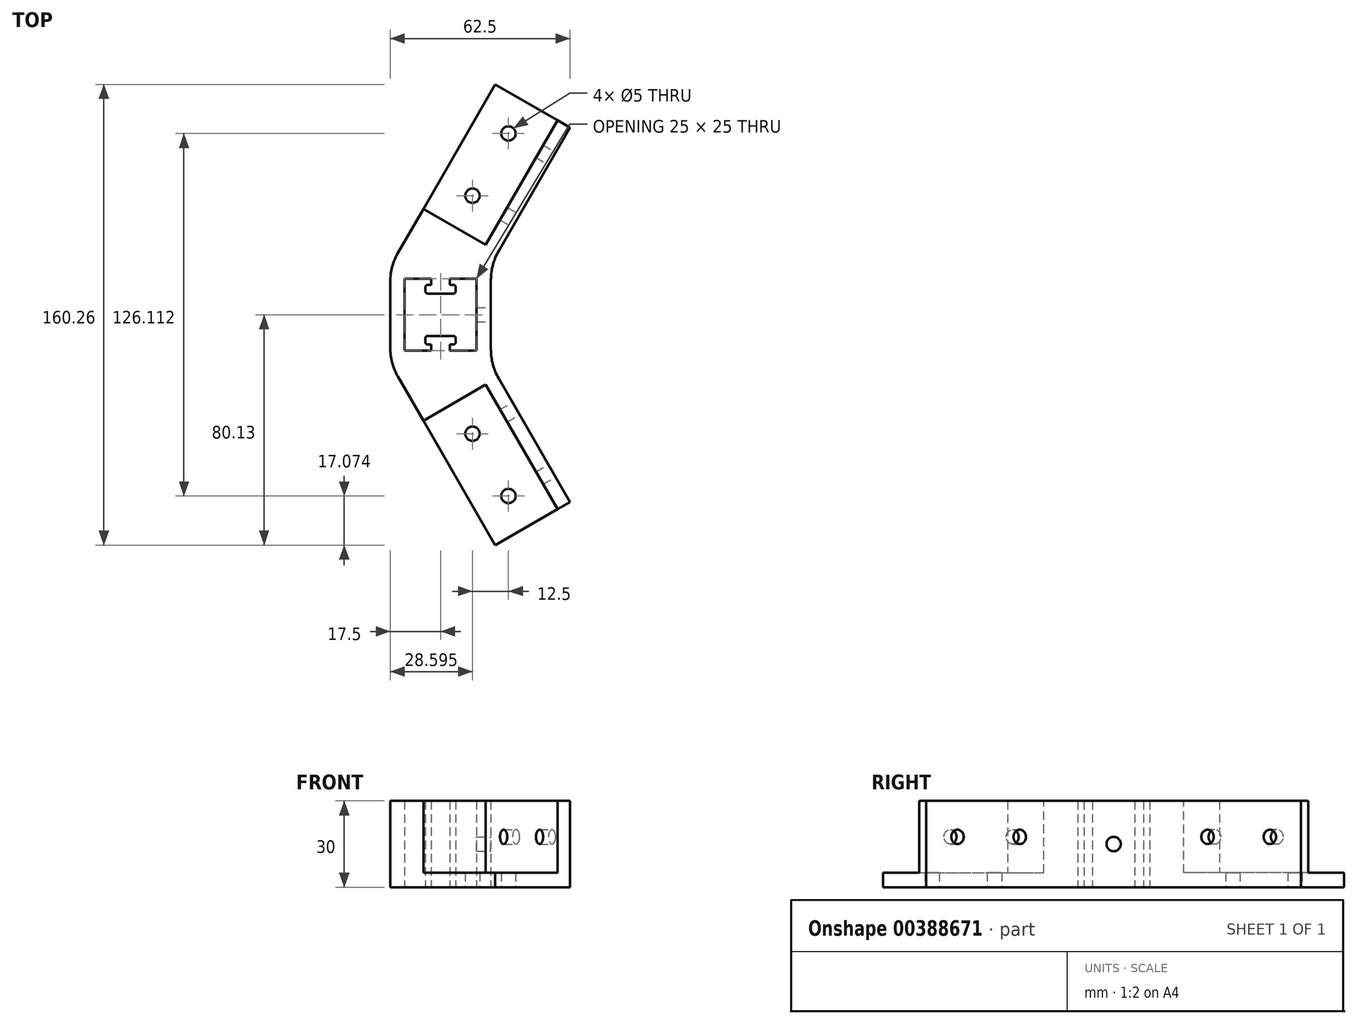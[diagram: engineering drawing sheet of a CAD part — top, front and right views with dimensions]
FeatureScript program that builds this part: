
annotation { "Feature Type Name" : "Feature", "Feature Type Description" : "" }
export const myFeature = defineFeature(function(context is Context, id is Id, definition is map)
    precondition{}
    {
        {
            var Q0;
            Q0=qCreatedBy(makeId("Top.planeOp"),FACE);
            var sketch = newSketch(context, id + "F0", { "sketchPlane" : qUnion([Q0])});
            skLineSegment(sketch, "E0", {"start": v(-35, 0) * mm, "end": v(-35, 16.88) * mm});
            skLineSegment(sketch, "E1", {"start": v(-35, 16.88) * mm, "end": v(-23.48, 36.83) * mm});
            skLineSegment(sketch, "E2", {"start": v(2.5, 21.83) * mm, "end": v(0, 17.5) * mm});
            skLineSegment(sketch, "E3", {"start": v(0, 17.5) * mm, "end": v(0, 0) * mm});
            skLineSegment(sketch, "E4", {"start": v(0, 0) * mm, "end": v(-5, 0) * mm});
            skLineSegment(sketch, "E5", {"start": v(0, 17.5) * mm, "end": v(-25.98, 32.5) * mm, "construction": true});
            skLineSegment(sketch, "E6", {"start": v(-35, 16.88) * mm, "end": v(0, 17.5) * mm, "construction": true});
            skLineSegment(sketch, "E7", {"start": v(0, 17.5) * mm, "end": v(-35, 17.5) * mm, "construction": true});
            skLineSegment(sketch, "E8", {"start": v(2.5, 21.83) * mm, "end": v(-23.48, 36.83) * mm});
            skLineSegment(sketch, "E9", {"start": v(-30, 0) * mm, "end": v(-30, 12.5) * mm});
            skLineSegment(sketch, "E10", {"start": v(-30, 12.5) * mm, "end": v(-20.75, 12.5) * mm});
            skLineSegment(sketch, "E11", {"start": v(-5, 12.5) * mm, "end": v(-5, 0) * mm});
            skLineSegment(sketch, "E12.trimOffspring", {"start": v(-30, 0) * mm, "end": v(-35, 0) * mm});
            skLineSegment(sketch, "E13", {"start": v(-20.75, 12.5) * mm, "end": v(-20.75, 10.37) * mm});
            skLineSegment(sketch, "E14", {"start": v(-20.75, 10.37) * mm, "end": v(-22, 10.37) * mm});
            skLineSegment(sketch, "E15", {"start": v(-22.75, 9.62) * mm, "end": v(-22.75, 8.12) * mm});
            skLineSegment(sketch, "E16", {"start": v(-22, 7.37) * mm, "end": v(-13, 7.37) * mm});
            skLineSegment(sketch, "E17", {"start": v(-12.25, 8.12) * mm, "end": v(-12.25, 9.62) * mm});
            skLineSegment(sketch, "E18", {"start": v(-13, 10.37) * mm, "end": v(-14.25, 10.37) * mm});
            skLineSegment(sketch, "E19", {"start": v(-14.25, 10.37) * mm, "end": v(-14.25, 12.5) * mm});
            skLineSegment(sketch, "E20.trimOffspring", {"start": v(-14.25, 12.5) * mm, "end": v(-5, 12.5) * mm});
            skPoint(sketch, "E21.visualSharp", {"position": v(-22.75, 10.37) * mm});
            skArc(sketch, "E21.filletArc", {"start": v(-22, 10.37) * mm, "mid": v(-22.53, 10.15) * mm, "end": v(-22.75, 9.62) * mm});
            skPoint(sketch, "E22.visualSharp", {"position": v(-22.75, 7.37) * mm});
            skArc(sketch, "E22.filletArc", {"start": v(-22.75, 8.12) * mm, "mid": v(-22.53, 7.59) * mm, "end": v(-22, 7.37) * mm});
            skPoint(sketch, "E23.visualSharp", {"position": v(-12.25, 10.37) * mm});
            skArc(sketch, "E23.filletArc", {"start": v(-12.25, 9.62) * mm, "mid": v(-12.47, 10.15) * mm, "end": v(-13, 10.37) * mm});
            skPoint(sketch, "E24.visualSharp", {"position": v(-12.25, 7.37) * mm});
            skArc(sketch, "E24.filletArc", {"start": v(-13, 7.37) * mm, "mid": v(-12.47, 7.59) * mm, "end": v(-12.25, 8.12) * mm});
            skSolve(sketch);
        }
        {
            var Q0;
            Q0=qSketchRegion(id+"F0",true);
            extrude(context, id + "F1", {"entities" : qUnion([Q0]), "depth" : 30 * mm});
        }
        {
            var Q0;
            Q0=makeQuery(id+"F1.opExtrude","SWEPT_FACE",FACE,{"disambiguationData":[OSD([sQuery(id+"F0.wireOp",EDGE,"E8")])]});
            var sketch = newSketch(context, id + "F2", { "sketchPlane" : qUnion([Q0])});
            skLineSegment(sketch, "E25", {"start": v(8.75, 30) * mm, "end": v(8.75, 0) * mm});
            skLineSegment(sketch, "E26", {"start": v(8.75, 0) * mm, "end": v(38.75, 0) * mm});
            skLineSegment(sketch, "E27", {"start": v(38.75, 0) * mm, "end": v(38.75, 5) * mm});
            skLineSegment(sketch, "E28", {"start": v(38.75, 5) * mm, "end": v(13.75, 5) * mm});
            skLineSegment(sketch, "E29", {"start": v(13.75, 5) * mm, "end": v(13.75, 30) * mm});
            skLineSegment(sketch, "E30", {"start": v(13.75, 30) * mm, "end": v(8.75, 30) * mm});
            skSolve(sketch);
        }
        {
            var Q0;
            Q0=qSketchRegion(id+"F2",true);
            extrude(context, id + "F3", {"entities" : qUnion([Q0]), "operationType" : NewBodyOperationType.ADD, "depth" : 50 * mm});
        }
        {
            var Q0;
            Q0=makeQuery(id+"F3.boolean.opBoolean","MERGE",FACE,{"derivedFrom":[makeQuery(id+"F1.opExtrude","CAP_FACE",FACE,{"disambiguationData":[OSD([sQuery(id+"F0.wireOp",EDGE,"E0"),sQuery(id+"F0.wireOp",EDGE,"E1"),sQuery(id+"F0.wireOp",EDGE,"E2"),sQuery(id+"F0.wireOp",EDGE,"E3"),sQuery(id+"F0.wireOp",EDGE,"E4"),sQuery(id+"F0.wireOp",EDGE,"E8"),sQuery(id+"F0.wireOp",EDGE,"E9"),sQuery(id+"F0.wireOp",EDGE,"E10"),sQuery(id+"F0.wireOp",EDGE,"E11"),sQuery(id+"F0.wireOp",EDGE,"E12.trimOffspring"),sQuery(id+"F0.wireOp",EDGE,"E13"),sQuery(id+"F0.wireOp",EDGE,"E14"),sQuery(id+"F0.wireOp",EDGE,"E15"),sQuery(id+"F0.wireOp",EDGE,"E16"),sQuery(id+"F0.wireOp",EDGE,"E17"),sQuery(id+"F0.wireOp",EDGE,"E18"),sQuery(id+"F0.wireOp",EDGE,"E19"),sQuery(id+"F0.wireOp",EDGE,"E20.trimOffspring"),sQuery(id+"F0.wireOp",EDGE,"E21.filletArc"),sQuery(id+"F0.wireOp",EDGE,"E22.filletArc"),sQuery(id+"F0.wireOp",EDGE,"E23.filletArc"),sQuery(id+"F0.wireOp",EDGE,"E24.filletArc")])],"isStart":true}),makeQuery(id+"F3.opExtrude","SWEPT_FACE",FACE,{"disambiguationData":[OSD([sQuery(id+"F2.wireOp",EDGE,"E26")])]})]});
            var sketch = newSketch(context, id + "F4", { "sketchPlane" : qUnion([Q0])});
            skPoint(sketch, "E31", {"position": v(6.1, -63.06) * mm});
            skPoint(sketch, "E32", {"position": v(-6.4, -41.4) * mm});
            skLineSegment(sketch, "E33", {"start": v(6.1, -63.06) * mm, "end": v(-6.4, -41.4) * mm, "construction": true});
            skSolve(sketch);
        }
        {
            var Q0;
            Q0=makeQuery(id+"F1.opExtrude","SWEPT_FACE",FACE,{"disambiguationData":[OSD([sQuery(id+"F0.wireOp",EDGE,"E3")])]});
            var sketch = newSketch(context, id + "F5", { "sketchPlane" : qUnion([Q0])});
            skPoint(sketch, "E34", {"position": v(0, 15) * mm});
            skSolve(sketch);
        }
        {
            var Q0;
            Q0=makeQuery(id+"F3.boolean.opBoolean","MERGE",FACE,{"derivedFrom":[makeQuery(id+"F1.opExtrude","SWEPT_FACE",FACE,{"disambiguationData":[OSD([sQuery(id+"F0.wireOp",EDGE,"E2")])]}),makeQuery(id+"F3.opExtrude","SWEPT_FACE",FACE,{"disambiguationData":[OSD([sQuery(id+"F2.wireOp",EDGE,"E25")])]})]});
            var sketch = newSketch(context, id + "F6", { "sketchPlane" : qUnion([Q0])});
            skPoint(sketch, "E35", {"position": v(32.66, 17.5) * mm});
            skPoint(sketch, "E36", {"position": v(57.66, 17.5) * mm});
            skLineSegment(sketch, "E37", {"start": v(32.66, 17.5) * mm, "end": v(57.66, 17.5) * mm, "construction": true});
            skSolve(sketch);
        }
        {
            var Q0;
            Q0=sQuery(id+"F5.wireOp",VERTEX,"E34");
            var Q1;
            Q1=sQuery(id+"F4.wireOp",VERTEX,"E32");
            var Q2;
            Q2=sQuery(id+"F4.wireOp",VERTEX,"E31");
            var Q3;
            Q3=sQuery(id+"F6.wireOp",VERTEX,"E35");
            var Q4;
            Q4=sQuery(id+"F6.wireOp",VERTEX,"E36");
            var Q5;
            Q5=makeQuery(id+"F1.opExtrude","SWEPT_BODY",BODY,{"disambiguationData":[OSD([sQuery(id+"F0.wireOp",EDGE,"E0"),sQuery(id+"F0.wireOp",EDGE,"E1"),sQuery(id+"F0.wireOp",EDGE,"E2"),sQuery(id+"F0.wireOp",EDGE,"E3"),sQuery(id+"F0.wireOp",EDGE,"E4"),sQuery(id+"F0.wireOp",EDGE,"E8"),sQuery(id+"F0.wireOp",EDGE,"E9"),sQuery(id+"F0.wireOp",EDGE,"E10"),sQuery(id+"F0.wireOp",EDGE,"E11"),sQuery(id+"F0.wireOp",EDGE,"E12.trimOffspring"),sQuery(id+"F0.wireOp",EDGE,"E13"),sQuery(id+"F0.wireOp",EDGE,"E14"),sQuery(id+"F0.wireOp",EDGE,"E15"),sQuery(id+"F0.wireOp",EDGE,"E16"),sQuery(id+"F0.wireOp",EDGE,"E17"),sQuery(id+"F0.wireOp",EDGE,"E18"),sQuery(id+"F0.wireOp",EDGE,"E19"),sQuery(id+"F0.wireOp",EDGE,"E20.trimOffspring"),sQuery(id+"F0.wireOp",EDGE,"E21.filletArc"),sQuery(id+"F0.wireOp",EDGE,"E22.filletArc"),sQuery(id+"F0.wireOp",EDGE,"E23.filletArc"),sQuery(id+"F0.wireOp",EDGE,"E24.filletArc")])]});
            hole(context, id + "F7", {"style" : HoleStyle.SIMPLE, "endStyle" : HoleEndStyle.BLIND, "standardTappedOrClearance" : lookupTablePath({ "standard" : "ISO", "size" : "5", "type" : "Drilled" }), "standardBlindInLast" : lookupTablePath({ "standard" : "ISO", "size" : "5", "type" : "Drilled" }), "holeDiameter" : 5 * mm, "holeDepth" : 12.7 * mm, "isTappedThrough" : true, "tappedDepth" : 12 * mm, "tapClearance" : 3, "locations" : qUnion([Q0, Q1, Q2, Q3, Q4]), "scope" : qUnion([Q5])});
        }
        {
            var Q0;
            Q0=makeQuery(id+"F1.opExtrude","SWEPT_EDGE",EDGE,{"disambiguationData":[OSD([sQuery(id+"F0.wireOp",EDGE,"E0"),sQuery(id+"F0.wireOp",EDGE,"E1")])]});
            var Q1;
            Q1=makeQuery(id+"F1.opExtrude","SWEPT_EDGE",EDGE,{"disambiguationData":[OSD([sQuery(id+"F0.wireOp",EDGE,"E2"),sQuery(id+"F0.wireOp",EDGE,"E3")])]});
            fillet(context, id + "F8", {"entities" : qUnion([Q0, Q1]), "radius" : 20 * mm, "tangentPropagation" : true, "allowEdgeOverflow" : false});
        }
        {
            var Q0;
            Q0=makeQuery(id+"F1.opExtrude","SWEPT_BODY",BODY,{"disambiguationData":[OSD([sQuery(id+"F0.wireOp",EDGE,"E0"),sQuery(id+"F0.wireOp",EDGE,"E1"),sQuery(id+"F0.wireOp",EDGE,"E2"),sQuery(id+"F0.wireOp",EDGE,"E3"),sQuery(id+"F0.wireOp",EDGE,"E4"),sQuery(id+"F0.wireOp",EDGE,"E8"),sQuery(id+"F0.wireOp",EDGE,"E9"),sQuery(id+"F0.wireOp",EDGE,"E10"),sQuery(id+"F0.wireOp",EDGE,"E11"),sQuery(id+"F0.wireOp",EDGE,"E12.trimOffspring"),sQuery(id+"F0.wireOp",EDGE,"E13"),sQuery(id+"F0.wireOp",EDGE,"E14"),sQuery(id+"F0.wireOp",EDGE,"E15"),sQuery(id+"F0.wireOp",EDGE,"E16"),sQuery(id+"F0.wireOp",EDGE,"E17"),sQuery(id+"F0.wireOp",EDGE,"E18"),sQuery(id+"F0.wireOp",EDGE,"E19"),sQuery(id+"F0.wireOp",EDGE,"E20.trimOffspring"),sQuery(id+"F0.wireOp",EDGE,"E21.filletArc"),sQuery(id+"F0.wireOp",EDGE,"E22.filletArc"),sQuery(id+"F0.wireOp",EDGE,"E23.filletArc"),sQuery(id+"F0.wireOp",EDGE,"E24.filletArc")])]});
            var Q1;
            Q1=qCreatedBy(makeId("Front.planeOp"),FACE);
            mirror(context, id + "F9", {"operationType" : NewBodyOperationType.ADD, "entities" : qUnion([Q0]), "mirrorPlane" : qUnion([Q1])});
        }
    });
